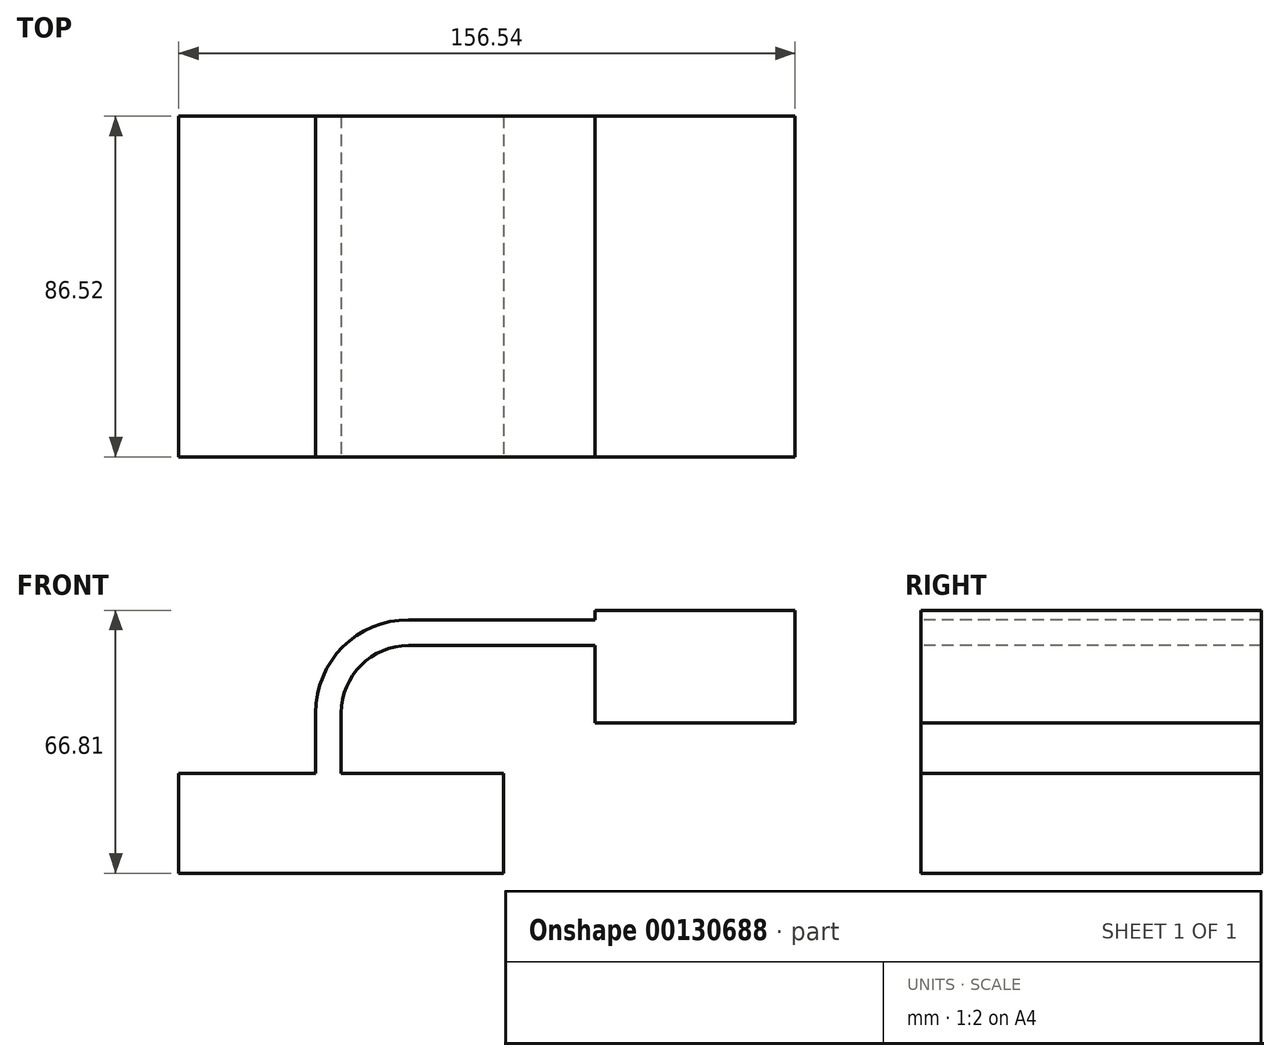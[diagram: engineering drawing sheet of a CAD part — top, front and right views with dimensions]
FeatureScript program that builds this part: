
annotation { "Feature Type Name" : "Feature", "Feature Type Description" : "" }
export const myFeature = defineFeature(function(context is Context, id is Id, definition is map)
    precondition{}
    {
        {
            var Q0;
            Q0=qCreatedBy(makeId("Front.planeOp"),FACE);
            var sketch = newSketch(context, id + "F0", { "sketchPlane" : qUnion([Q0])});
            skLineSegment(sketch, "E0.bottom", {"start": v(-41.28, 12.7) * mm, "end": v(41.28, 12.7) * mm});
            skLineSegment(sketch, "E0.top", {"start": v(-41.28, -12.7) * mm, "end": v(41.28, -12.7) * mm});
            skLineSegment(sketch, "E0.left", {"start": v(-41.28, 12.7) * mm, "end": v(-41.28, -12.7) * mm});
            skLineSegment(sketch, "E0.right", {"start": v(41.28, 12.7) * mm, "end": v(41.28, -12.7) * mm});
            skPoint(sketch, "E0.middle", {"position": v(0, 0) * mm});
            skLineSegment(sketch, "E1.bottom", {"start": v(35.62, 67.37) * mm, "end": v(34.79, 67.37) * mm});
            skLineSegment(sketch, "E1.top", {"start": v(35.62, 67.64) * mm, "end": v(34.79, 67.64) * mm});
            skLineSegment(sketch, "E1.left", {"start": v(35.62, 67.37) * mm, "end": v(35.62, 67.64) * mm});
            skLineSegment(sketch, "E1.right", {"start": v(34.79, 67.37) * mm, "end": v(34.79, 67.64) * mm});
            skLineSegment(sketch, "E2.bottom", {"start": v(34.79, 67.37) * mm, "end": v(35.62, 67.37) * mm});
            skLineSegment(sketch, "E2.top", {"start": v(34.79, 67.64) * mm, "end": v(35.62, 67.64) * mm});
            skLineSegment(sketch, "E3.bottom", {"start": v(64.47, 54.11) * mm, "end": v(115.27, 54.11) * mm});
            skLineSegment(sketch, "E3.top", {"start": v(64.47, 25.54) * mm, "end": v(115.27, 25.54) * mm});
            skLineSegment(sketch, "E3.left", {"start": v(64.47, 54.11) * mm, "end": v(64.47, 25.54) * mm});
            skLineSegment(sketch, "E3.right", {"start": v(115.27, 54.11) * mm, "end": v(115.27, 25.54) * mm});
            skPoint(sketch, "E3.middle", {"position": v(89.87, 39.83) * mm});
            skLineSegment(sketch, "E4", {"start": v(0, 12.7) * mm, "end": v(0, 28.02) * mm});
            skArc(sketch, "E5", {"start": v(0, 28.02) * mm, "mid": v(5.02, 40.15) * mm, "end": v(17.15, 45.17) * mm});
            skLineSegment(sketch, "E6", {"start": v(17.14, 45.17) * mm, "end": v(86.68, 45.17) * mm});
            skLineSegment(sketch, "E7.0", {"start": v(17.14, 51.7) * mm, "end": v(86.68, 51.7) * mm});
            skArc(sketch, "E7.1", {"start": v(-6.52, 28.02) * mm, "mid": v(0.4, 44.76) * mm, "end": v(17.15, 51.7) * mm});
            skLineSegment(sketch, "E7.2", {"start": v(-6.52, 12.7) * mm, "end": v(-6.52, 28.02) * mm});
            skSolve(sketch);
        }
        {
            var Q0;
            {var subQ6=sQuery(id+"F0.wireOp",EDGE,"E4");Q0=makeQuery(id+"F0.imprint","IMPRINT",FACE,{"disambiguationData":[TD([[makeQuery(id+"F0.imprint","IMPRINT",EDGE,{"derivedFrom":subQ6}),1.0]])]});}
            var Q1;
            Q1=makeQuery(id+"F0.imprint","IMPRINT",FACE,{"disambiguationData":[TD([[makeQuery(id+"F0.imprint","IMPRINT",EDGE,{"derivedFrom":sQuery(id+"F0.wireOp",EDGE,"E0.top")}),1.0]])]});
            var Q2;
            {var subQ3=sQuery(id+"F0.wireOp",EDGE,"E3.bottom");Q2=makeQuery(id+"F0.imprint","IMPRINT",FACE,{"disambiguationData":[TD([[makeQuery(id+"F0.imprint","IMPRINT",EDGE,{"derivedFrom":subQ3}),-1.0]])]});}
            extrude(context, id + "F1", {"entities" : qUnion([Q0, Q1, Q2]), "endBound" : BoundingType.SYMMETRIC, "oppositeDirection" : true, "depth" : 86.51 * mm});
        }
    });
